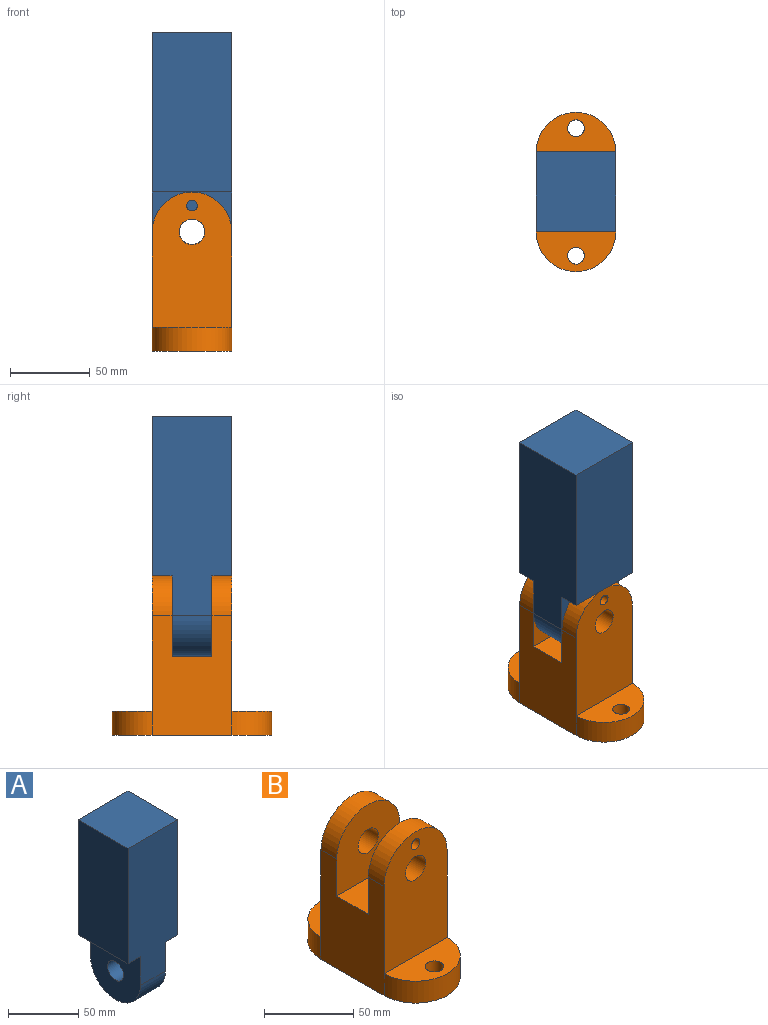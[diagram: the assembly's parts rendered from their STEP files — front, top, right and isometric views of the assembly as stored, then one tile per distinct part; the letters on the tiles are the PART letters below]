
ASSEMBLY  parts=2 mates=1
PART A: 11 faces, bbox 50x50x150 mm
  f0: plane 50x50mm, normal (1,0,0), area 2030.7mm2, adj f2,f3,f5,f9,f10
  f1: plane 50x50mm, normal (-1,0,0), area 2030.7mm2, adj f3,f5,f8,f9,f10
  f2: plane 50x12.5mm, normal (0,0,-1), area 625mm2, adj f0,f3,f4,f5
  f3: plane 125x50mm, normal (0,-1,0), area 5625mm2, adj f0,f1,f2,f4,f6,f7,f8,f9
  f4: plane 100x50mm, normal (1,0,0), area 5000mm2, adj f2,f3,f5,f7
  f5: plane 125x50mm, normal (0,1,0), area 5625mm2, adj f0,f1,f2,f4,f6,f7,f8,f9
  f6: plane 100x50mm, normal (-1,0,0), area 5000mm2, adj f3,f5,f7,f8
  f7: plane 50x50mm, normal (0,0,1), area 2500mm2, adj f3,f4,f5,f6
  f8: plane 50x12.5mm, normal (0,0,-1), area 625mm2, adj f1,f3,f5,f6
  f9: cylinder r=25mm len=50mm, axis (-1,0,0), area 1963.5mm2, adj f0,f1,f3,f5
  f10: cylinder r=8mm len=25mm, axis (-1,0,0), area 1256.6mm2, adj f0,f1
PART B: 19 faces, bbox 50x100x100 mm
  f0: plane 85x50mm, normal (0,1,0), area 3780.7mm2, adj f4,f5,f8,f15,f17
  f1: plane 85x50mm, normal (0,-1,0), area 3744.4mm2, adj f4,f5,f10,f14,f16,f18
  f2: plane 50.5x50mm, normal (0,-1,0), area 2055.7mm2, adj f4,f5,f13,f15,f17
  f3: plane 50.5x50mm, normal (0,1,0), area 2019.4mm2, adj f4,f5,f13,f14,f16,f18
  f4: plane 75x50mm, normal (-1,0,0), area 3112.5mm2, adj f0,f1,f2,f3,f6,f7,f9,f13
  f5: plane 75x50mm, normal (1,0,0), area 3112.5mm2, adj f0,f1,f2,f3,f6,f7,f9,f13
  f6: plane 100x50mm, normal (0,0,-1), area 4290.3mm2, adj f4,f5,f7,f9,f11,f12
  f7: cylinder r=25mm len=50mm, axis (0,0,-1), area 1178.1mm2, adj f4,f5,f6,f8
  f8: plane 50x25mm, normal (0,0,1), area 895.2mm2, adj f0,f7,f12
  f9: cylinder r=25mm len=50mm, axis (0,0,-1), area 1178.1mm2, adj f4,f5,f6,f10
  f10: plane 50x25mm, normal (0,0,1), area 895.2mm2, adj f1,f9,f11
  f11: cylinder r=5.25mm len=15mm, axis (0,0,-1), area 494.8mm2, adj f6,f10
  f12: cylinder r=5.25mm len=15mm, axis (0,0,-1), area 494.8mm2, adj f6,f8
  f13: plane 50x25mm, normal (0,0,1), area 1250mm2, adj f2,f3,f4,f5
  f14: cylinder r=25mm len=50mm, axis (0,-1,0), area 981.7mm2, adj f1,f3,f4,f5
  f15: cylinder r=25mm len=50mm, axis (0,-1,0), area 981.7mm2, adj f0,f2,f4,f5
  f16: cylinder r=8mm len=16mm, axis (0,-1,0), area 628.3mm2, adj f1,f3
  f17: cylinder r=8mm len=16mm, axis (0,-1,0), area 628.3mm2, adj f0,f2
  f18: cylinder r=3.4mm len=12.5mm, axis (0,-1,0), area 267mm2, adj f1,f3
PLACE A rot(axis=(0,0,1),90deg) t=(-44.4,7.76,100.1)mm
PLACE B t=(-44.4,7.76,0.1)mm
MATE slider A.f10 <-> B.f14  axis (0,1,0) through (-44.4,20.26,75.1)mm
